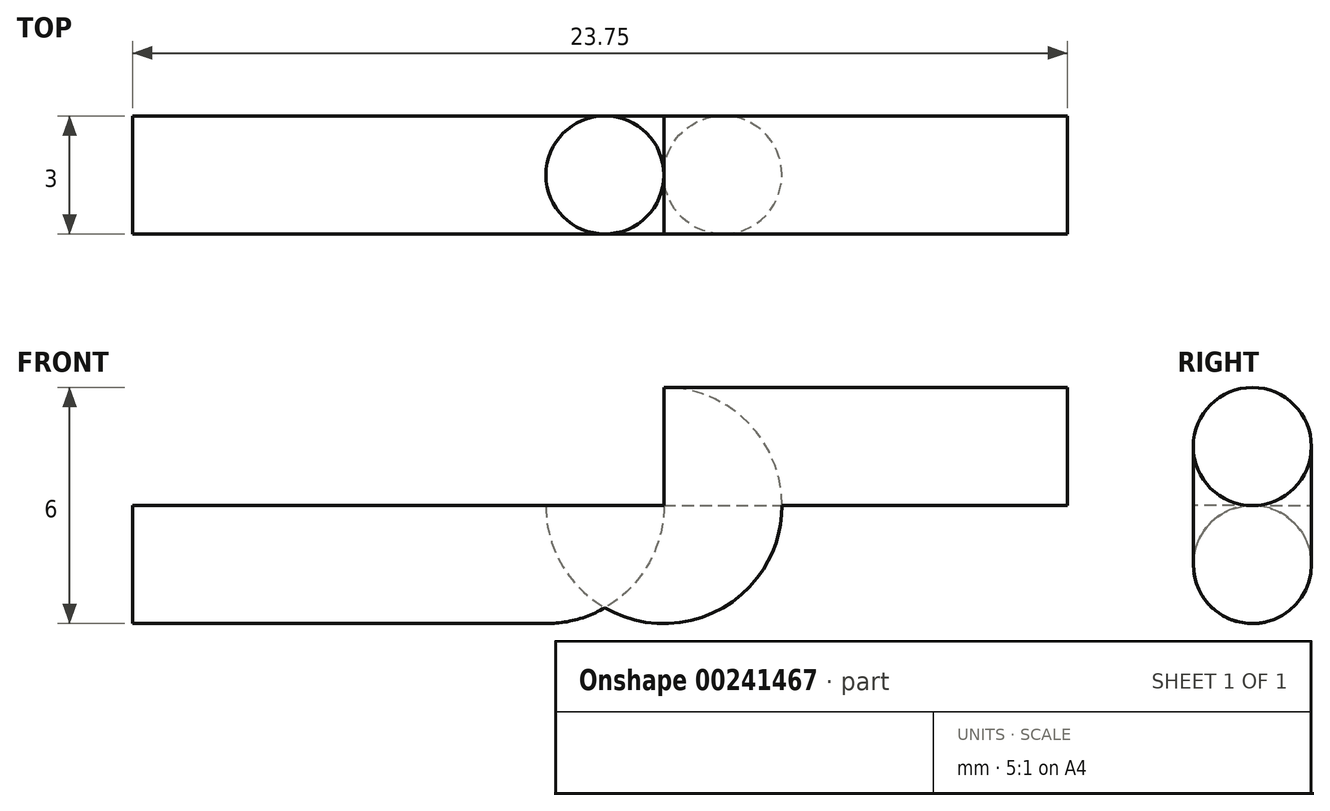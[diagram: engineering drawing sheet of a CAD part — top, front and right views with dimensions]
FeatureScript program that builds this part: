
annotation { "Feature Type Name" : "Feature", "Feature Type Description" : "" }
export const myFeature = defineFeature(function(context is Context, id is Id, definition is map)
    precondition{}
    {
        {
            var Q0;
            Q0=qCreatedBy(makeId("Front.planeOp"),FACE);
            var sketch = newSketch(context, id + "F0", { "sketchPlane" : qUnion([Q0])});
            skLineSegment(sketch, "E0", {"start": v(-12, 0) * mm, "end": v(11.84, 0) * mm, "construction": true});
            skLineSegment(sketch, "E1", {"start": v(-11.96, 3) * mm, "end": v(11.75, 3) * mm, "construction": true});
            skArc(sketch, "E2", {"start": v(-1.5, 0) * mm, "mid": v(-0.44, 0.44) * mm, "end": v(0, 1.5) * mm});
            skArc(sketch, "E3", {"start": v(1.5, 3) * mm, "mid": v(0.44, 2.56) * mm, "end": v(0, 1.5) * mm});
            skLineSegment(sketch, "E4", {"start": v(11.75, 3) * mm, "end": v(1.5, 3) * mm});
            skLineSegment(sketch, "E5", {"start": v(-12, 0) * mm, "end": v(-1.5, 0) * mm});
            skLineSegment(sketch, "E6", {"start": v(-10.53, -5.73) * mm, "end": v(13.67, -5.73) * mm, "construction": true});
            skArc(sketch, "E7", {"start": v(1.5, -5.73) * mm, "mid": v(0.44, -6.17) * mm, "end": v(0, -7.23) * mm});
            skArc(sketch, "E8", {"start": v(-3.02, -11.73) * mm, "mid": v(-0.83, -10.8) * mm, "end": v(0, -8.57) * mm});
            skLineSegment(sketch, "E9", {"start": v(13.67, -5.73) * mm, "end": v(1.5, -5.73) * mm});
            skLineSegment(sketch, "E10", {"start": v(-10.53, -11.7) * mm, "end": v(-3.02, -11.73) * mm});
            skLineSegment(sketch, "E11", {"start": v(0, -8.91) * mm, "end": v(0, -7.23) * mm});
            skSolve(sketch);
        }
        {
            var Q0;
            Q0=sQuery(id+"F0.wireOp",VERTEX,"E5.start");
            var Q1;
            Q1=qCreatedBy(makeId("Right.planeOp"),FACE);
            cPlane(context, id + "F1", {"entities" : qUnion([Q0, Q1]), "cplaneType" : CPlaneType.PLANE_POINT, "offset" : 25 * mm, "width" : 150 * mm, "height" : 150 * mm});
        }
        {
            var Q0;
            Q0=qCreatedBy(id+"F1.planeOp",FACE);
            var sketch = newSketch(context, id + "F2", { "sketchPlane" : qUnion([Q0])});
            skCircle(sketch, "E12", {"center": v(0, 0) * mm, "radius": 1.5 * mm});
            skSolve(sketch);
        }
        {
            var Q0;
            Q0=makeQuery(id+"F2.imprint","IMPRINT",FACE,{"disambiguationData":[TD([[makeQuery(id+"F2.imprint","IMPRINT",EDGE,{"derivedFrom":sQuery(id+"F2.wireOp",EDGE,"E12")}),1.0]])]});
            var Q1;
            Q1=sQuery(id+"F0.wireOp",EDGE,"E5");
            var Q2;
            Q2=sQuery(id+"F0.wireOp",EDGE,"E2");
            var Q3;
            Q3=sQuery(id+"F0.wireOp",EDGE,"E3");
            var Q4;
            Q4=sQuery(id+"F0.wireOp",EDGE,"E4");
            sweep(context, id + "F3", {"profiles" : qUnion([Q0]), "path" : qUnion([Q1, Q2, Q3, Q4])});
        }
    });
